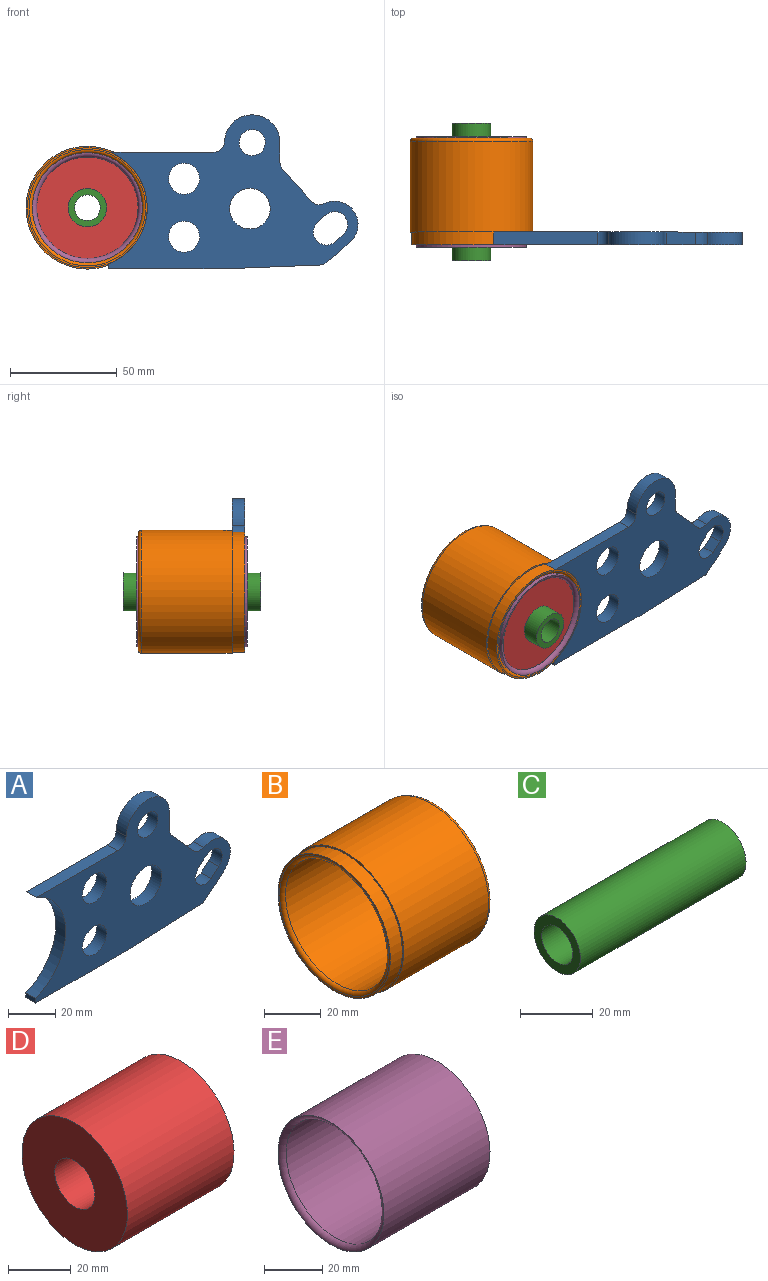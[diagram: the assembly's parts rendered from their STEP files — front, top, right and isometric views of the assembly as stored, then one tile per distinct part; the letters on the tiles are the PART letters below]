
ASSEMBLY  parts=5 mates=4
PART A: 25 faces, bbox 116.7x6x72 mm
  f0: plane 9.5x6mm, normal (1,0,0), area 57mm2, adj f1,f22,f23,f24
  f1: cylinder r=13mm len=25.99mm, axis (0,-1,0), area 240.7mm2, adj f0,f2,f23,f24
  f2: cylinder r=5mm len=6mm, axis (0,-1,0), area 46.3mm2, adj f1,f3,f23,f24
  f3: plane 48.65x6mm, normal (0,0,1), area 291.9mm2, adj f2,f4,f23,f24
  f4: cylinder r=28.05mm len=52.2mm, axis (0,-1,0), area 402.5mm2, adj f3,f5,f23,f24
  f5: plane 6x2.3mm, normal (-1,0,0), area 13.8mm2, adj f4,f6,f23,f24
  f6: plane 56.82x6mm, normal (0,0,-1), area 340.9mm2, adj f5,f7,f23,f24
  f7: plane 42.8x6mm, normal (0.04,0,-1), area 257mm2, adj f6,f8,f23,f24
  f8: cylinder r=2mm len=6mm, axis (0,-1,0), area 7.5mm2, adj f7,f9,f23,f24
  f9: plane 7.79x6.11mm, normal (0.62,0,-0.79), area 59.4mm2, adj f8,f10,f23,f24
  f10: plane 6x4.63mm, normal (0.68,0,-0.73), area 37.8mm2, adj f9,f11,f23,f24
  f11: cylinder r=11mm len=19.08mm, axis (0,-1,0), area 188.8mm2, adj f10,f12,f23,f24
  f12: cylinder r=5mm len=6mm, axis (0,-1,0), area 39.2mm2, adj f11,f13,f23,f24
  f13: plane 14.96x13.36mm, normal (0.75,0,0.67), area 120.3mm2, adj f12,f22,f23,f24
  f14: cylinder r=6.1mm len=10.65mm, axis (0,-1,0), area 115.6mm2, adj f15,f21,f23,f24
  f15: plane 6x4.62mm, normal (-0.67,0,0.75), area 37.2mm2, adj f14,f16,f23,f24
  f16: cylinder r=6.1mm len=10.58mm, axis (0,-1,0), area 108.3mm2, adj f15,f21,f23,f24
  f17: cylinder r=6.1mm len=12.2mm, axis (0,-1,0), area 230mm2, adj f23,f24
  f18: cylinder r=9.5mm len=19mm, axis (0,-1,0), area 358.1mm2, adj f23,f24
  f19: cylinder r=7.25mm len=14.5mm, axis (0,-1,0), area 273.3mm2, adj f23,f24
  f20: cylinder r=7.25mm len=14.5mm, axis (0,-1,0), area 273.3mm2, adj f23,f24
  f21: plane 6x3.81mm, normal (0.68,0,-0.73), area 31.1mm2, adj f14,f16,f23,f24
  f22: cylinder r=5mm len=6mm, axis (0,-1,0), area 21.9mm2, adj f0,f13,f23,f24
  f23: plane 116.73x72mm, normal (0,1,0), area 4219mm2, adj f0,f1,f2,f3,f4,f5,f6,f7
  f24: plane 116.73x72mm, normal (0,-1,0), area 4219mm2, adj f0,f1,f2,f3,f4,f5,f6,f7
PART B: 7 faces, bbox 50x62.2x62.2 mm
  f0: cylinder r=25.75mm len=51.5mm, axis (-1,0,0), area 7604.2mm2, adj f5,f6
  f1: cylinder r=28.75mm len=57.5mm, axis (-1,0,0), area 7677.3mm2, adj f4,f6
  f2: plane 56.1x56.1mm, normal (-1,0,0), area 139mm2, adj f3,f5
  f3: cylinder r=28.05mm len=56.1mm, axis (-1,0,0), area 1057.5mm2, adj f2,f4
  f4: plane 57.5x57.5mm, normal (-1,0,0), area 124.9mm2, adj f1,f3
  f5: torus R=27.25mm, axis (1,0,0), area 389.3mm2, adj f0,f2
  f6: torus R=27.25mm, axis (1,0,0), area 806.8mm2, adj f0,f1
PART C: 4 faces, bbox 64.2x18x18 mm
  f0: cylinder r=6mm len=64.2mm, axis (-1,0,0), area 2420.3mm2, adj f2,f3
  f1: cylinder r=9mm len=64.2mm, axis (-1,0,0), area 3630.4mm2, adj f2,f3
  f2: plane 18x18mm, normal (1,0,0), area 141.4mm2, adj f0,f1
  f3: plane 18x18mm, normal (-1,0,0), area 141.4mm2, adj f0,f1
PART D: 4 faces, bbox 48x47.5x47.5 mm
  f0: cylinder r=9mm len=48mm, axis (-1,0,0), area 2714.3mm2, adj f2,f3
  f1: cylinder r=23.75mm len=48mm, axis (-1,0,0), area 7162.8mm2, adj f2,f3
  f2: plane 47.5x47.5mm, normal (1,0,0), area 1517.6mm2, adj f0,f1
  f3: plane 47.5x47.5mm, normal (-1,0,0), area 1517.6mm2, adj f0,f1
PART E: 4 faces, bbox 51.6x58.8x58.8 mm
  f0: cylinder r=23.75mm len=47.6mm, axis (-1,0,0), area 7103.1mm2, adj f2,f3
  f1: cylinder r=25.75mm len=51.6mm, axis (-1,0,0), area 8348.5mm2, adj f2,f3
  f2: torus R=25.75mm, axis (1,0,0), area 483.2mm2, adj f0,f1
  f3: torus R=25.75mm, axis (1,0,0), area 483.2mm2, adj f0,f1
PLACE A t=(22.88,-77.3,22.8)mm
PLACE B rot(axis=(0,0,1),90deg) t=(-113.73,-77.3,51.31)mm
PLACE C rot(axis=(0,0,1),90deg) t=(-113.73,-52.55,51.31)mm
PLACE D rot(axis=(0,0,1),90deg) t=(-113.73,-52.55,51.31)mm
PLACE E rot(axis=(0,0,1),90deg) t=(-113.73,-52.55,51.31)mm
MATE fastened A.f4 <-> B.f3  axis (0,1,0) through (-113.73,-71.3,51.31)mm
MATE fastened D.f1 <-> E.f0  axis (0,-1,0) through (-113.73,-52.55,51.31)mm
MATE fastened C.f1 <-> D.f0  axis (0,-1,0) through (-113.73,-52.55,51.31)mm
MATE fastened E.f1 <-> B.f1  axis (0,-1,0) through (-113.73,-52.55,51.31)mm
